# Revit family: Cassettes à splicer
name_source: partatom
category: Installations électriques
units: mm (PartAtom-declared; Revit-internal decimal feet)

## family parameters
Basée sur le plan de construction = Non
Conserver l'orientation des annotations = Non
Cote de connecteur circulaire = Utiliser le diamètre
Couper avec des vides une fois chargée = Non
Partagée = Non
Point de calcul de pièce = Non
Toujours verticalement = Oui
Type d'élément = Normal

## types (8) — shared parameters
Classe ETIM = EC002699
Couleur = IDS_NOIR
Croisé = Non
Fonction = Cassettes pré-équipées
Hauteur = 43.7 mm  [stored 0.143373 ft]
Largeur (mm) = 110 mm  [stored 0.360892 ft]
Lien e-catalogue = https://www.legrand.fr
Profondeur = 185 mm  [stored 0.606955 ft]
Température de fonctionnement = -10°C à 60°C
Température de stockage = -10°C à 60°C
Type de connecteur interne = Autre
zero-valued in all types: Elévation par défaut, Nombre de connecteurs face arrière

## per-type parameters (varying)
| type | Classe de fibre optique | Connecteurs LC | Connecteurs SC | EAN | Nombre de connecteurs face avant | Référence Legrand | Type de connecteur externe | Visibilité connecteurs LC | Visibilité connecteurs SC |
| Cassette pré-équipée SC duplex 6 fibres multimode | OM4 | IDS_CONNECTEURS_LC_A_SPLICER : Bloc LC 6 fibres multimode | Connecteurs LC à splicer : Bloc SC 6 fibres multimode | 3414971400337 | 6 | 032180 | SC_DUPLEX | Non | Oui |
| Cassette pré-équipée LC duplex 6 fibres multimode | OM4 | IDS_CONNECTEURS_LC_A_SPLICER : Bloc LC 6 fibres multimode | Connecteurs LC à splicer : Bloc SC 6 fibres monomode | 3414971400351 | 6 | 032181 | LC_DUPLEX | Oui | Non |
| Cassette pré-équipée SC duplex 12 fibres multimode | OM4 | IDS_CONNECTEURS_LC_A_SPLICER : Bloc LC 6 fibres monomode | Connecteurs LC à splicer : Bloc SC 12 fibres multimode | 3414971400375 | 12 | 032182 | SC_DUPLEX | Non | Oui |
| Cassette pré-équipée LC duplex 12 fibres multimode | OM4 | IDS_CONNECTEURS_LC_A_SPLICER : Bloc LC 12 fibres multimode | Connecteurs LC à splicer : Bloc SC 6 fibres monomode | 3414971400399 | 12 | 032183 | LC_DUPLEX | Oui | Non |
| Cassette pré-équipée SC duplex 6 fibres monomode | OS2 | IDS_CONNECTEURS_LC_A_SPLICER : Bloc LC 6 fibres monomode | Connecteurs LC à splicer : Bloc SC 6 fibres monomode | 3414971400412 | 6 | 032184 | SC_DUPLEX | Non | Oui |
| Cassette pré-équipée LC duplex 6 fibres monomode | OS2 | IDS_CONNECTEURS_LC_A_SPLICER : Bloc LC 6 fibres monomode | Connecteurs LC à splicer : Bloc SC 6 fibres monomode | 3414971400436 | 6 | 032185 | LC_DUPLEX | Oui | Non |
| Cassette pré-équipée SC duplex 12 fibres monomode | OS2 | IDS_CONNECTEURS_LC_A_SPLICER : Bloc LC 6 fibres monomode | Connecteurs LC à splicer : Bloc SC 12 fibres monomode | 3414971400450 | 12 | 032186 | SC_DUPLEX | Non | Oui |
| Cassette pré-équipée LC duplex 12 fibres monomode | OS2 | IDS_CONNECTEURS_LC_A_SPLICER : Bloc LC 12 fibres monomode | Connecteurs LC à splicer : Bloc SC 6 fibres monomode | 3414971400474 | 12 | 032187 | LC_DUPLEX | Oui | Non |

note: column(s) folded — value = type name in every type: Libellé BIM

note: [stored X ft] marks values corroborated as IEEE doubles in the binary element streams (Revit-internal decimal feet)
